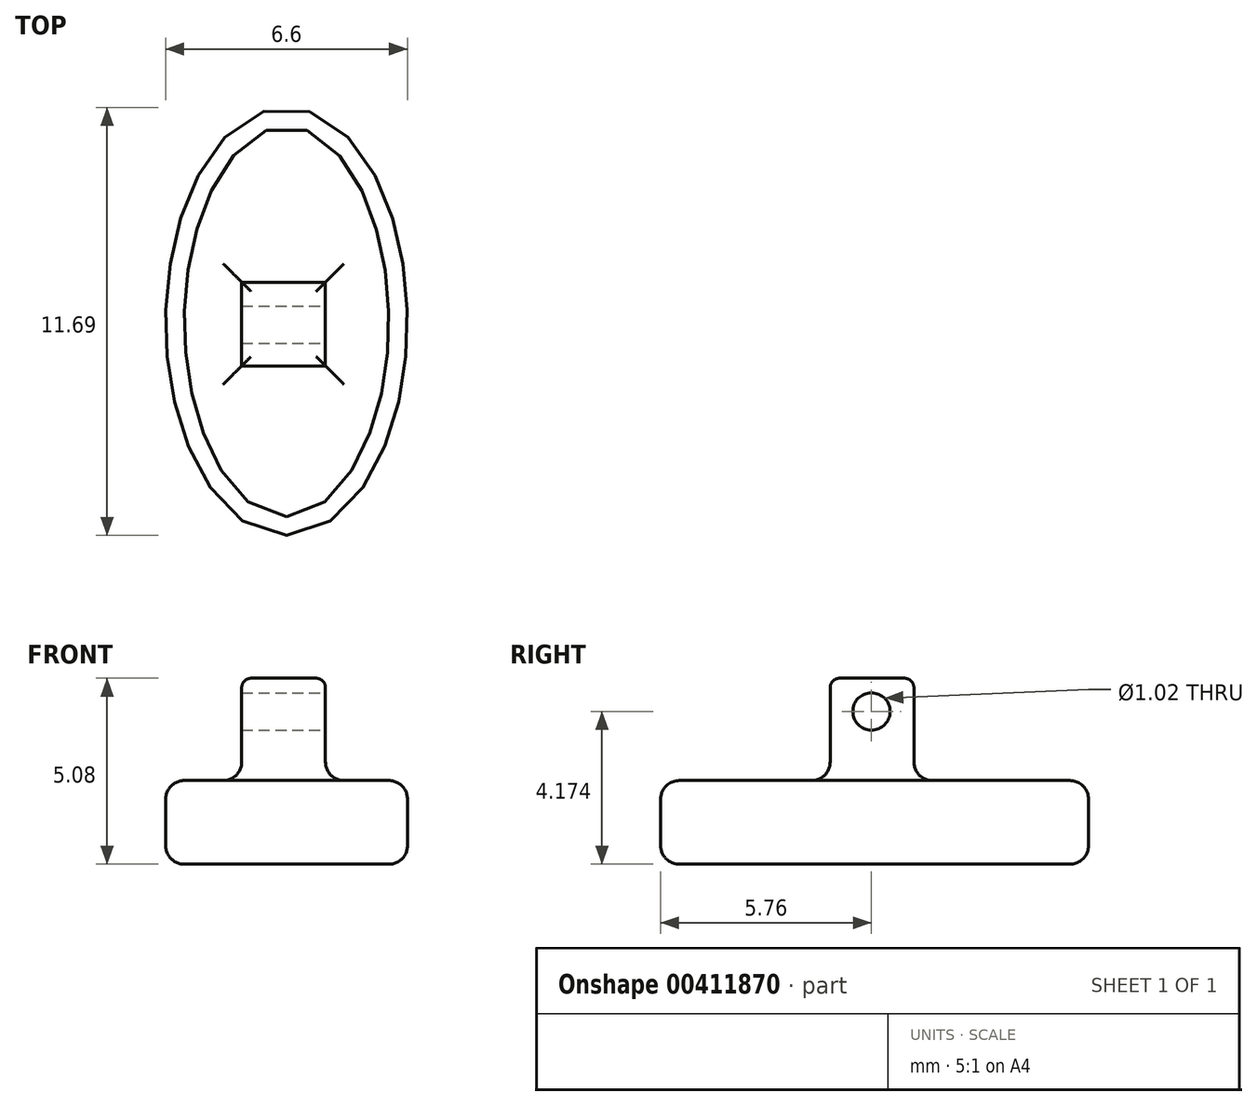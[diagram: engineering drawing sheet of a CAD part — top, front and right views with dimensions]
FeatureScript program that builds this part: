
annotation { "Feature Type Name" : "Feature", "Feature Type Description" : "" }
export const myFeature = defineFeature(function(context is Context, id is Id, definition is map)
    precondition{}
    {
        {
            var Q0;
            Q0=qCreatedBy(makeId("Top.planeOp"),FACE);
            var sketch = newSketch(context, id + "F0", { "sketchPlane" : qUnion([Q0])});
            skEllipse(sketch, "E0", {"center": v(0.08, 0.09) * mm, "majorRadius": 5.84 * mm, "minorRadius": 3.3 * mm, "majorAxis": v(0, -1)});
            skSolve(sketch);
        }
        {
            var Q0;
            Q0=qCreatedBy(makeId("Right.planeOp"),FACE);
            var sketch = newSketch(context, id + "F1", { "sketchPlane" : qUnion([Q0])});
            skLineSegment(sketch, "E1.bottom", {"start": v(1.16, 5.08) * mm, "end": v(-1.13, 5.08) * mm});
            skLineSegment(sketch, "E1.top", {"start": v(1.16, 0) * mm, "end": v(-1.13, 0) * mm});
            skLineSegment(sketch, "E1.left", {"start": v(1.16, 5.08) * mm, "end": v(1.16, 0) * mm});
            skLineSegment(sketch, "E1.right", {"start": v(-1.13, 5.08) * mm, "end": v(-1.13, 0) * mm});
            skSolve(sketch);
        }
        {
            var Q0;
            Q0=makeQuery(id+"F0.imprint","IMPRINT",FACE,{"disambiguationData":[TD([[makeQuery(id+"F0.imprint","IMPRINT",EDGE,{"derivedFrom":sQuery(id+"F0.wireOp",EDGE,"E0")}),1.0]])]});
            extrude(context, id + "F2", {"entities" : qUnion([Q0]), "depth" : 2.3 * mm});
        }
        {
            var Q0;
            Q0=makeQuery(id+"F1.imprint","IMPRINT",FACE,{"disambiguationData":[TD([[makeQuery(id+"F1.imprint","IMPRINT",EDGE,{"derivedFrom":sQuery(id+"F1.wireOp",EDGE,"E1.bottom")}),1.0]])]});
            extrude(context, id + "F3", {"entities" : qUnion([Q0]), "operationType" : NewBodyOperationType.ADD, "endBound" : BoundingType.SYMMETRIC, "depth" : 2.3 * mm});
        }
        {
            var Q0;
            Q0=makeQuery(id+"F3.opExtrude","CAP_FACE",FACE,{"disambiguationData":[OSD([sQuery(id+"F1.wireOp",EDGE,"E1.bottom"),sQuery(id+"F1.wireOp",EDGE,"E1.top"),sQuery(id+"F1.wireOp",EDGE,"E1.left"),sQuery(id+"F1.wireOp",EDGE,"E1.right")])],"isStart":false});
            var sketch = newSketch(context, id + "F4", { "sketchPlane" : qUnion([Q0])});
            skCircle(sketch, "E2", {"center": v(0, 4.17) * mm, "radius": 0.5 * mm});
            skSolve(sketch);
        }
        {
            var Q0;
            Q0=sQuery(id+"F4.wireOp",VERTEX,"E2.center");
            var Q1;
            Q1=makeQuery(id+"F2.opExtrude","SWEPT_BODY",BODY,{"disambiguationData":[OSD([sQuery(id+"F0.wireOp",EDGE,"E0")])]});
            hole(context, id + "F5", {"style" : HoleStyle.SIMPLE, "endStyle" : HoleEndStyle.THROUGH, "holeDiameter" : 1.02 * mm, "isTappedThrough" : true, "tappedDepth" : 12.7 * mm, "tapClearance" : 3, "locations" : qUnion([Q0]), "scope" : qUnion([Q1])});
        }
        {
            var Q0;
            Q0=makeQuery(id+"F2.opExtrude","CAP_FACE",FACE,{"disambiguationData":[OSD([sQuery(id+"F0.wireOp",EDGE,"E0")])],"isStart":true});
            fillet(context, id + "F6", {"entities" : qUnion([Q0]), "radius" : 0.5 * mm, "tangentPropagation" : true, "allowEdgeOverflow" : false});
        }
        {
            var Q0;
            Q0=makeQuery(id+"F3.opExtrude","SWEPT_FACE",FACE,{"disambiguationData":[OSD([sQuery(id+"F1.wireOp",EDGE,"E1.bottom")])]});
            fillet(context, id + "F7", {"entities" : qUnion([Q0]), "radius" : 0.25 * mm, "tangentPropagation" : true, "allowEdgeOverflow" : false});
        }
        {
            var Q0;
            Q0=makeQuery(id+"F2.opExtrude","CAP_FACE",FACE,{"disambiguationData":[OSD([sQuery(id+"F0.wireOp",EDGE,"E0")])],"isStart":false});
            fillet(context, id + "F8", {"entities" : qUnion([Q0]), "radius" : 0.5 * mm, "tangentPropagation" : true, "allowEdgeOverflow" : false});
        }
    });
